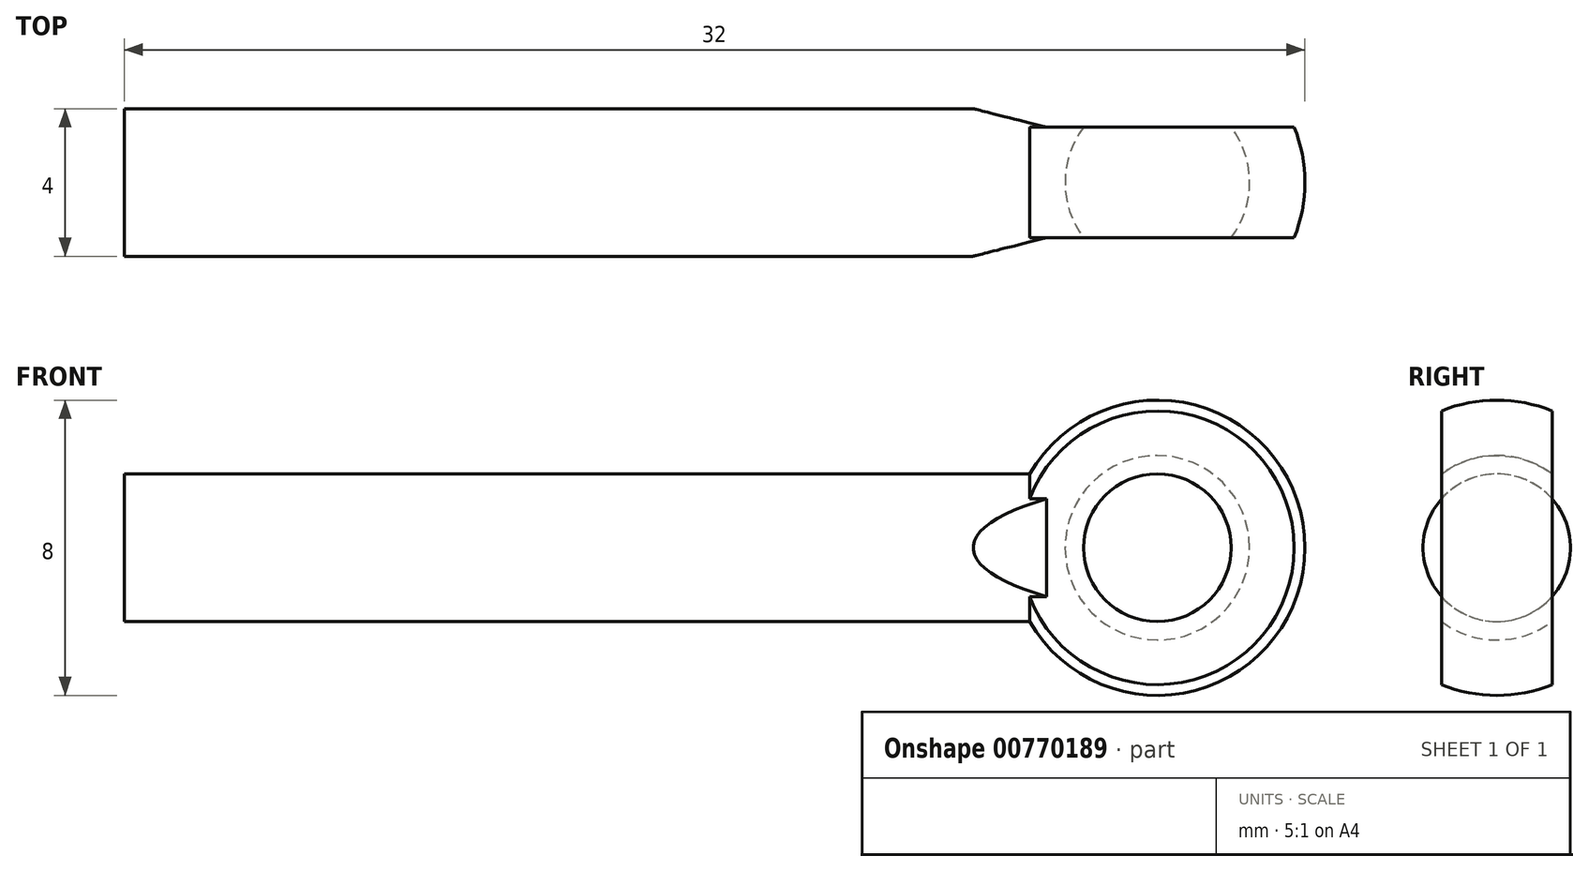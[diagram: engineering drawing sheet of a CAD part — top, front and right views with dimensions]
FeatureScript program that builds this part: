
annotation { "Feature Type Name" : "Feature", "Feature Type Description" : "" }
export const myFeature = defineFeature(function(context is Context, id is Id, definition is map)
    precondition{}
    {
        {
            var Q0;
            Q0=qCreatedBy(makeId("Top.planeOp"),FACE);
            var sketch = newSketch(context, id + "F0", { "sketchPlane" : qUnion([Q0])});
            skArc(sketch, "E0", {"start": v(0, 2.5) * mm, "mid": v(-2.5, 0) * mm, "end": v(0, -2.5) * mm});
            skArc(sketch, "E1", {"start": v(0, 4) * mm, "mid": v(-4, 0) * mm, "end": v(0, -4) * mm});
            skLineSegment(sketch, "E2", {"start": v(0, 4) * mm, "end": v(0, -4) * mm});
            skSolve(sketch);
        }
        {
            var Q0;
            {var subQ0=sQuery(id+"F0.wireOp",EDGE,"E0");Q0=makeQuery(id+"F0.imprint","IMPRINT",FACE,{"disambiguationData":[TD([[makeQuery(id+"F0.imprint","IMPRINT",EDGE,{"derivedFrom":subQ0}),-1.0]])]});}
            var Q1;
            Q1=sQuery(id+"F0.wireOp",EDGE,"E2");
            revolve(context, id + "F1", {"surfaceOperationType" : NewSurfaceOperationType.NEW, "entities" : qUnion([Q0]), "axis" : qUnion([Q1]), "revolveType" : RevolveType.FULL});
        }
        {
            var Q0;
            Q0=qCreatedBy(makeId("Top.planeOp"),FACE);
            var sketch = newSketch(context, id + "F2", { "sketchPlane" : qUnion([Q0])});
            skLineSegment(sketch, "E3.bottom", {"start": v(-5, 1.5) * mm, "end": v(5, 1.5) * mm});
            skLineSegment(sketch, "E3.top", {"start": v(-5, -1.5) * mm, "end": v(5, -1.5) * mm});
            skLineSegment(sketch, "E3.left", {"start": v(-5, 1.5) * mm, "end": v(-5, -1.5) * mm});
            skLineSegment(sketch, "E3.right", {"start": v(5, 1.5) * mm, "end": v(5, -1.5) * mm});
            skSolve(sketch);
        }
        {
            var Q0;
            Q0=makeQuery(id+"F2.imprint","IMPRINT",FACE,{"disambiguationData":[TD([[makeQuery(id+"F2.imprint","IMPRINT",EDGE,{"derivedFrom":sQuery(id+"F2.wireOp",EDGE,"E3.bottom")}),-1.0]])]});
            extrude(context, id + "F3", {"entities" : qUnion([Q0]), "operationType" : NewBodyOperationType.INTERSECT, "endBound" : BoundingType.SYMMETRIC, "depth" : 25 * mm, "offsetDistance" : 25 * mm});
        }
        {
            var Q0;
            Q0=qCreatedBy(makeId("Right.planeOp"),FACE);
            cPlane(context, id + "F4", {"entities" : qUnion([Q0]), "cplaneType" : CPlaneType.OFFSET, "offset" : 3 * mm, "oppositeDirection" : true, "width" : 150 * mm, "height" : 150 * mm});
        }
        {
            var Q0;
            Q0=qCreatedBy(id+"F4.planeOp",FACE);
            var sketch = newSketch(context, id + "F5", { "sketchPlane" : qUnion([Q0])});
            skCircle(sketch, "E4", {"center": v(0, 0) * mm, "radius": 2 * mm});
            skSolve(sketch);
        }
        {
            var Q0;
            Q0=makeQuery(id+"F5.imprint","IMPRINT",FACE,{"disambiguationData":[TD([[makeQuery(id+"F5.imprint","IMPRINT",EDGE,{"derivedFrom":sQuery(id+"F5.wireOp",EDGE,"E4")}),1.0]])]});
            extrude(context, id + "F6", {"entities" : qUnion([Q0]), "operationType" : NewBodyOperationType.ADD, "oppositeDirection" : true, "depth" : 25 * mm, "offsetDistance" : 25 * mm});
        }
        {
            var Q0;
            Q0=qCreatedBy(makeId("Top.planeOp"),FACE);
            var sketch = newSketch(context, id + "F7", { "sketchPlane" : qUnion([Q0])});
            skLineSegment(sketch, "E5", {"start": v(-3, 1.5) * mm, "end": v(-5, 2) * mm});
            skLineSegment(sketch, "E6", {"start": v(-5, -2) * mm, "end": v(-3, -1.5) * mm});
            skLineSegment(sketch, "E7", {"start": v(-5, 2) * mm, "end": v(10, 2) * mm});
            skLineSegment(sketch, "E8", {"start": v(10, 2) * mm, "end": v(10, -2) * mm});
            skLineSegment(sketch, "E9", {"start": v(10, -2) * mm, "end": v(-5, -2) * mm});
            skLineSegment(sketch, "E10", {"start": v(-3, -1.5) * mm, "end": v(-3, 1.5) * mm});
            skLineSegment(sketch, "E11", {"start": v(-3, -2) * mm, "end": v(-28, -2) * mm});
            skLineSegment(sketch, "E12", {"start": v(-28, 2) * mm, "end": v(-3, 2) * mm});
            skArc(sketch, "E13", {"start": v(3.7, -1.5) * mm, "mid": v(4, 0) * mm, "end": v(3.7, 1.5) * mm});
            skLineSegment(sketch, "E14", {"start": v(-3, 1.5) * mm, "end": v(9, 1.5) * mm});
            skLineSegment(sketch, "E15", {"start": v(9, 1.5) * mm, "end": v(9, -1.5) * mm});
            skLineSegment(sketch, "E16", {"start": v(9, -1.5) * mm, "end": v(-3, -1.5) * mm});
            skSolve(sketch);
        }
        {
            var Q0;
            {var subQ5=sQuery(id+"F7.wireOp",EDGE,"E5");Q0=makeQuery(id+"F7.imprint","IMPRINT",FACE,{"disambiguationData":[TD([[makeQuery(id+"F7.imprint","IMPRINT",EDGE,{"derivedFrom":subQ5}),-1.0]])]});}
            extrude(context, id + "F8", {"entities" : qUnion([Q0]), "operationType" : NewBodyOperationType.REMOVE, "endBound" : BoundingType.SYMMETRIC, "oppositeDirection" : true, "depth" : 25 * mm, "offsetDistance" : 25 * mm});
        }
    });
